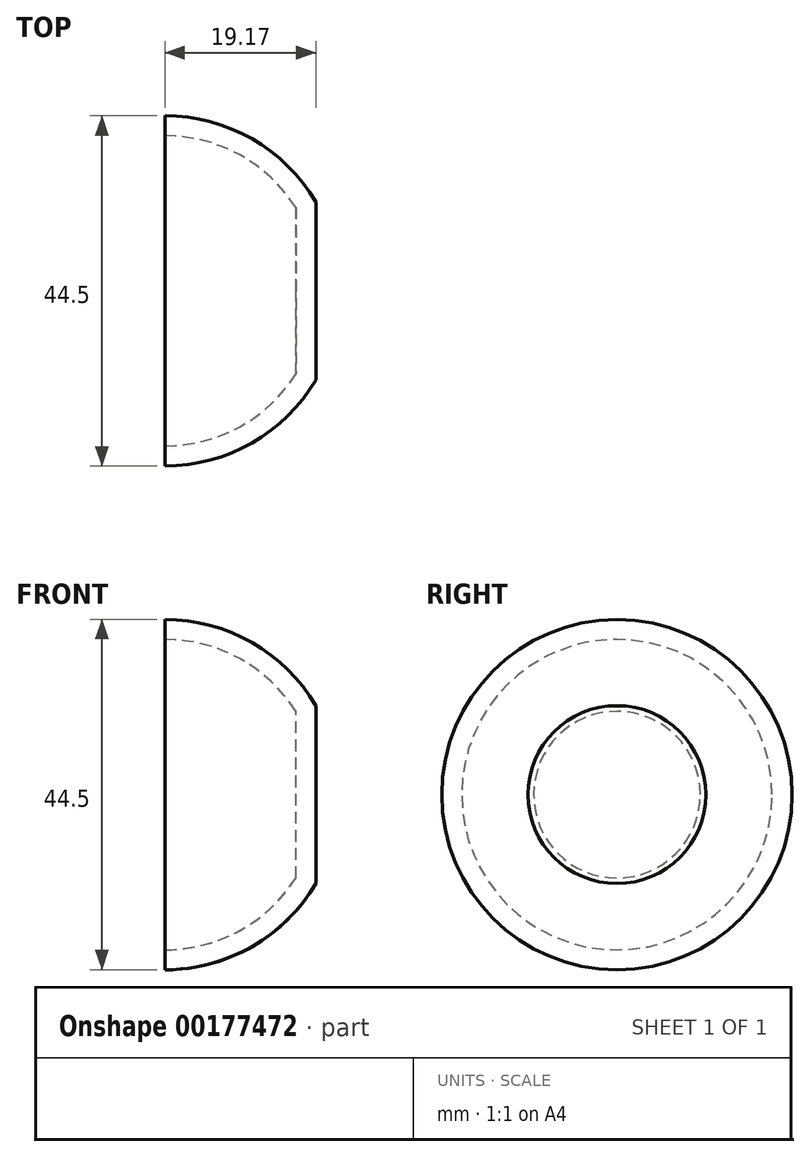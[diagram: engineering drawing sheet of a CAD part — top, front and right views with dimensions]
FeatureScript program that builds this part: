
annotation { "Feature Type Name" : "Feature", "Feature Type Description" : "" }
export const myFeature = defineFeature(function(context is Context, id is Id, definition is map)
    precondition{}
    {
        {
            var Q0;
            Q0=qCreatedBy(makeId("Top.planeOp"),FACE);
            var sketch = newSketch(context, id + "F0", { "sketchPlane" : qUnion([Q0])});
            skLineSegment(sketch, "E0", {"start": v(1.05, 0) * mm, "end": v(20.22, 0) * mm});
            skArc(sketch, "E1", {"start": v(20.22, 11.3) * mm, "mid": v(12.1, 19.32) * mm, "end": v(1.05, 22.25) * mm});
            skLineSegment(sketch, "E2", {"start": v(1.05, 0) * mm, "end": v(1.05, 22.25) * mm});
            skPoint(sketch, "E3.orphan", {"position": v(-21.2, 0) * mm});
            skLineSegment(sketch, "E4", {"start": v(20.22, 0) * mm, "end": v(20.22, 11.3) * mm});
            skSolve(sketch);
        }
        {
            var Q0;
            Q0=makeQuery(id+"F0.imprint","IMPRINT",FACE,{"disambiguationData":[TD([[makeQuery(id+"F0.imprint","IMPRINT",EDGE,{"derivedFrom":sQuery(id+"F0.wireOp",EDGE,"E0")}),1.0]])]});
            var Q1;
            Q1=sQuery(id+"F0.wireOp",EDGE,"E0");
            revolve(context, id + "F1", {"entities" : qUnion([Q0]), "axis" : qUnion([Q1]), "revolveType" : RevolveType.FULL, "oppositeDirection" : true});
        }
        {
            var Q0;
            Q0=makeQuery(id+"F1.opRevolve","SWEPT_FACE",FACE,{"disambiguationData":[OSD([sQuery(id+"F0.wireOp",EDGE,"E2")])]});
            shell(context, id + "F2", {"entities" : qUnion([Q0]), "thickness" : 2.54 * mm});
        }
    });
